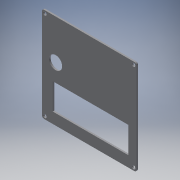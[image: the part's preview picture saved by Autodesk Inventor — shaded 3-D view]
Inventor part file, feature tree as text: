
AUTODESK INVENTOR PART (.ipt)
format: ipt  version: 2019 (Build 230136000, 136)  size: 134,656 bytes
history: native  units: mm
features: reference x5, other x3, extrude x2, sketch x2, fillet x1
ambient origin geometry x8: Origin, YZ Plane, XZ Plane, XY Plane, X Axis, Y Axis, Z Axis, Center Point
bodies: Solid1 (feature_tree)
feature tree (13):
  extrude  "Extrusion1"  Depth=90.0mm
  fillet  "Fillet1"  Radius=72.0mm
  extrude  "Extrusion2"  Depth=2.0mm
  sketch  "Sketch1"  dims[d0=90.0mm d1=90.0mm d2=72.0mm]
  reference  "Reference1"
  sketch  "Sketch2"  dims[d3=25.0mm d4=7.5mm d5=5.0mm d6=12.5mm d9=1.5mm d10=0.0mm d11=2.0mm d12=3.3mm d13=3.3mm d14=3.3mm d15=3.3mm d16=3.0mm d17=0.0mm d19=38.0mm d20=13.0mm]
  reference  "Reference2"
  reference  "Reference3"
  reference  "Reference4"
  reference  "Reference5"
  other  "<userpath>\Desktop\not_drawing_sys\cad\Assembly1.iam"
  other  "Assembly1.iam"
  other  "base:1"
